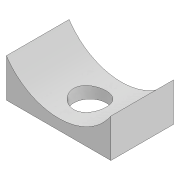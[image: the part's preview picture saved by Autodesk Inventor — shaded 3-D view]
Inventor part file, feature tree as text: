
AUTODESK INVENTOR PART (.ipt)
format: ipt  version: 2022 (Build 260153000, 153)  size: 100,864 bytes
history: native  units: mm
features: extrude x2, sketch x2, projected_geometry x1
ambient origin geometry x8: Origin, YZ Plane, XZ Plane, XY Plane, X Axis, Y Axis, Z Axis, Center Point
bodies: Solid1 (feature_tree)
feature tree (5):
  extrude  "Extrusion1"  Depth=1.0mm
  extrude  "Extrusion2"  Depth=6.0mm
  sketch  "Sketch1"  dims[d0=12.0mm d1=1.0mm]
  sketch  "Sketch2"  dims[d2=5.0mm d3=5.0mm d4=6.0mm d5=0.0mm d6=3.1mm d7=6.0mm d8=0.0mm]
  projected_geometry  "Projected Loop1"
